# Revit family: Gira_5565925
name_source: partatom
category: Elektroinstallationen
revit_build: Autodesk Revit 2018 (Build: 20170223_1515(x64)
units: mm (PartAtom-declared; Revit-internal decimal feet)

## family parameters
Arbeitsebenenbasiert = Ja
Beim Laden mit Abzugskörper schneiden = Nein
Bemaßung runder Anschluss = Durchmesser verwenden
Beschriftungsausrichtung beibehalten = Nein
Gemeinsam genutzt = Nein
Immer vertikal = Nein
Raumberechnungspunkt = Nein
Teiletyp = Normal

## types (1)
- Türstationsmodul System 106 Schwarz matt
    Anzahl der Klingeltasten = 1
    Ausführung = sprechen/klingeln
    BIMSITE_PRODUCT_ID = 2001b05bddc416c8632d500e7e53bb465c2a9e29
    Beschreibung = System 106 Türstationsmodul. Das Gira System 106 ist ein Installationssystem aus Echtmetall in puristisch-edlem Design ohne Rahmen, basierend auf einem Grundmaß von 106,5 × 106,5 mm und einer geringen Aufbauhöhe von 28,7 mm. Mit der modularen Türstation im Gira System 106 beginnt Gastlichkeit schon vor der Haustür. Von Ruftasten-, Sprach- und Kameramodul bis hin zum Info- und Blindmodul präsentieren sich alle Funktionen in einem stimmigen Gesamtbild. Im Dunkeln sorgen die hinterleuchteten Ruftasten mit Beschriftungsfeld für gute Lesbarkeit und eine ansprechende Erscheinung.  Individuell anpassbar durch modularen Aufbau Das System 106 kann in Ein-und Mehrfamilienhäusern, aber auch in Bürogebäuden, Industrieobjekten und Hotels eingesetzt werden. Der modulare Aufbau ermöglicht es, das System in Größe, Design und Funktionalität individuell an den jeweiligen Bedarf anzupassen. Erweiterungen und Änderungen sind durch Modulaustausch jederzeit einfach möglich. Selbst ein reiner Frontwechsel ist mit dem System möglich. Somit kann das Erscheinungsbild der Anlage auch nachträglich von z. B. Verkehrsweiß auf die Oberfläche Edelstahl geändert werden, ohne dabei die Elektronikeinheiten mit tauschen zu müssen.  Hochwertige Materialien Die Module sind rahmenlos mit Echtmaterial-Designfronten in zwei gebürsteten Edelstahlvarianten (V2A und V4A), eloxiertem Aluminium C-0 und einer verkehrsweiß (RAL 9016) lackierten Metalllegierung erhältlich: robuste Materialien, die für Langlebigkeit sorgen. Kamera- und Anzeigemodul (DIN 18040) verfügen über eine Schwarzglasabdeckung.  Einfache Installation und stufenweise Montage Das System kann parallel zum Baufortschritt in verschiedenen Stufen installiert werden. So ist es möglich, beim Rohbau zunächst nur den unteren Teil des Aufputz-Gehäuses zu montieren, Leitungen und Module können dann hinzugefügt werden, wenn sie gebraucht werden.  Individuelle Beschriftungsmöglichkeiten Ruftasten- und Info-Module können über den Gira Beschriftungsservice individuell laserbeschriftet werden.  Merkmale:  Kompaktes Sprachmodul mit integriertem Ruftaster für die Kommunikation zwischen innen und außen.  Ein hochwertiges Mikrofon und ein wetterfester Lautsprecher sorgen für gute Verständigung.  Spannungsversorgung über 2-Draht Bus. Zusätzlicher Anschluss für ZV (z. B. notwendig ab 3. Kameramodul).  Alle anderen System 106 Module (außer Sprachmodul) werden über das Türstationsmodul mit Spannung versorgt.  Hinweise :  Professionelle Beschriftung über den Gira Beschriftungsservice www.beschriftung.gira.de.
    Breite [mm] = 106.5
    Datenblatt = https://media.live.bim.site
    Farbe = schwarz
    Funktion PTZ (Schwenken/Neigen/Zoomen) = Nein
    GTIN = 4010337100676
    HAN = 5565925
    HeinzeBIM = https://www.heinze.de
    Hersteller = Gira
    Höhe [mm] = 106.5
    Hörgerätekompatibel = Nein
    Installationstechnik = Bus-System
    Ist System = Nein
    Ist Zubehör = Nein
    Kosten = 0 $
    Manuell einstellbare Kamera = Nein
    Material_1 = MT_Black
    Material_2 = MT_White
    Material_3 = MT_Black
    Produktseite = https://media.live.bim.site
    Typname = Türstationsmodul System 106 Schwarz matt
    URL = https://www.gira.de
    Vorgabe-Ansicht = 1219 mm

## geometry (parser evidence)
native form markers: Sweep x3
no freeform markers — native parametric forms only
